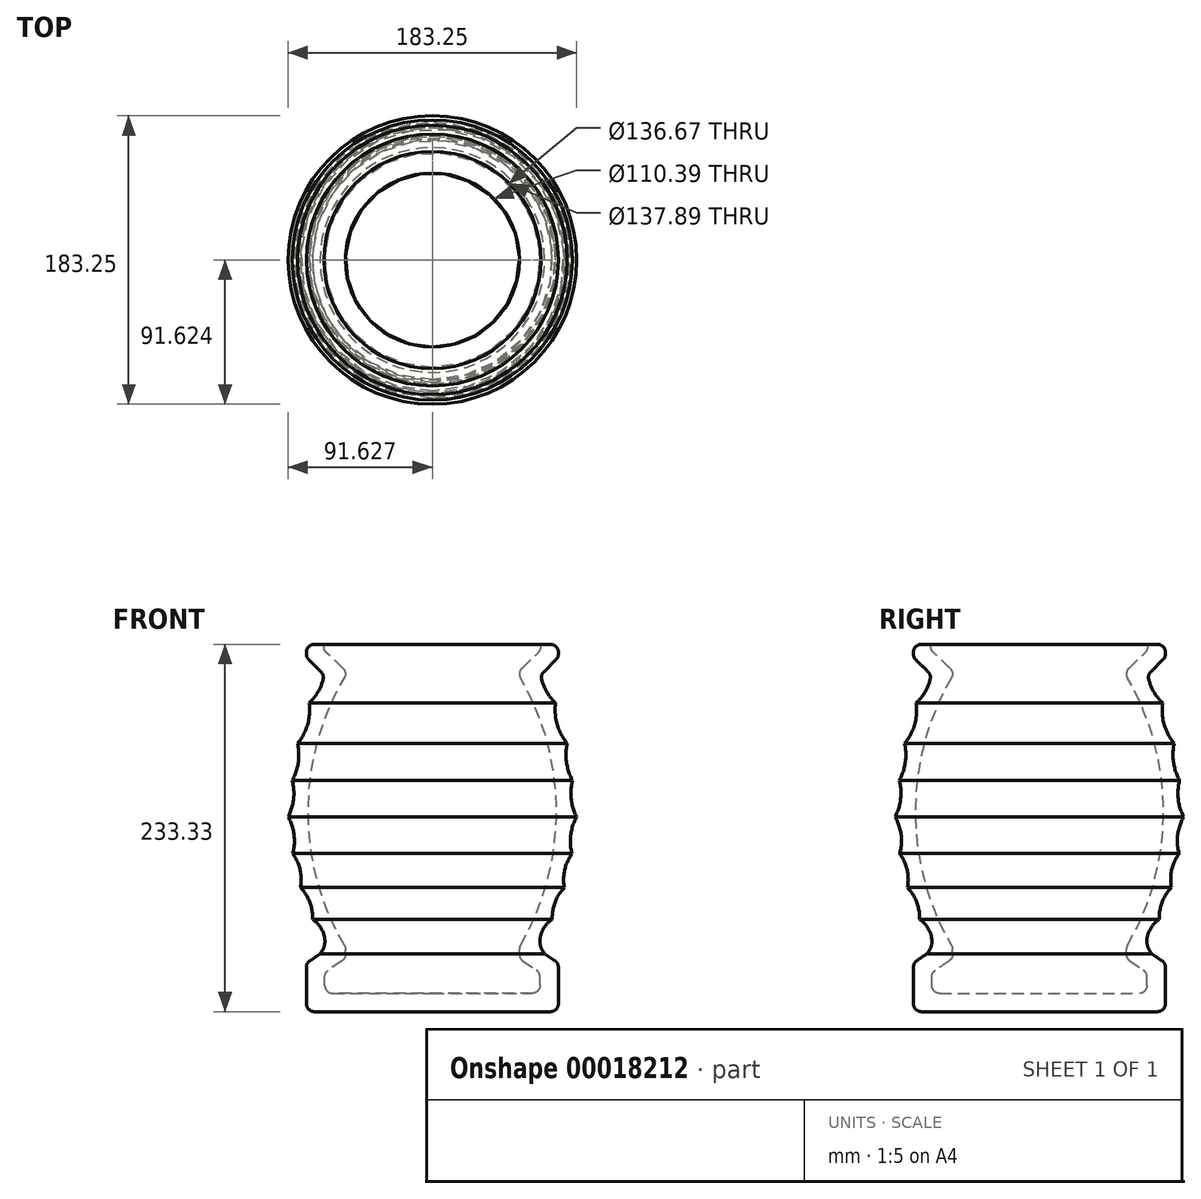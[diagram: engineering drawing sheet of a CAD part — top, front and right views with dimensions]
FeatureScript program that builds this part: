
annotation { "Feature Type Name" : "Feature", "Feature Type Description" : "" }
export const myFeature = defineFeature(function(context is Context, id is Id, definition is map)
    precondition{}
    {
        {
            var Q0;
            Q0=qCreatedBy(makeId("Top.planeOp"),FACE);
            var sketch = newSketch(context, id + "F0", { "sketchPlane" : qUnion([Q0])});
            skLineSegment(sketch, "E0.top", {"start": v(-71, -103.34) * mm, "end": v(4, -103.34) * mm});
            skLineSegment(sketch, "E1", {"start": v(-76, 125) * mm, "end": v(-76, 123.78) * mm});
            skLineSegment(sketch, "E2", {"start": v(-74.51, 120.22) * mm, "end": v(-66.76, 112.58) * mm});
            skLineSegment(sketch, "E3", {"start": v(-76, -98.34) * mm, "end": v(-76, -75.05) * mm});
            skLineSegment(sketch, "E4", {"start": v(-73.82, -70.91) * mm, "end": v(-67.37, -66.52) * mm});
            skLineSegment(sketch, "E5.1", {"start": v(-64.34, -86.67) * mm, "end": v(-64.34, -81.21) * mm});
            skLineSegment(sketch, "E5.2", {"start": v(-62.15, -77.08) * mm, "end": v(-53.38, -71.1) * mm});
            skLineSegment(sketch, "E5.4", {"start": v(-63.4, 124.87) * mm, "end": v(-52.8, 114.77) * mm});
            skArc(sketch, "E5.5", {"start": v(-51.92, 108.64) * mm, "mid": v(-74.82, 23.66) * mm, "end": v(-51.87, -61.3) * mm});
            skLineSegment(sketch, "E5.6", {"start": v(-51.2, -66.97) * mm, "end": v(-51.2, -63.81) * mm});
            skArc(sketch, "E6", {"start": v(-74.28, 92.72) * mm, "mid": v(-68.68, 99.63) * mm, "end": v(-65.4, 107.9) * mm});
            skArc(sketch, "E7", {"start": v(-81.6, 67.04) * mm, "mid": v(-75.23, 79.1) * mm, "end": v(-74.28, 92.72) * mm});
            skLineSegment(sketch, "E8", {"start": v(-64.95, 128.5) * mm, "end": v(-64.95, 128.95) * mm});
            skLineSegment(sketch, "E9", {"start": v(-71, 130) * mm, "end": v(-65.99, 130) * mm});
            skLineSegment(sketch, "E10", {"start": v(-59.34, -91.67) * mm, "end": v(4, -91.67) * mm});
            skLineSegment(sketch, "E11", {"start": v(4, -91.67) * mm, "end": v(4, -103.34) * mm});
            skArc(sketch, "E12", {"start": v(-84.98, 43.55) * mm, "mid": v(-81.2, 55) * mm, "end": v(-81.6, 67.04) * mm});
            skArc(sketch, "E13", {"start": v(-87.63, 20.25) * mm, "mid": v(-84.19, 31.66) * mm, "end": v(-84.98, 43.55) * mm});
            skArc(sketch, "E14", {"start": v(-72.12, -44.65) * mm, "mid": v(-73.9, -33.8) * mm, "end": v(-79.8, -24.54) * mm});
            skArc(sketch, "E15", {"start": v(-79.8, -24.54) * mm, "mid": v(-80.06, -13.23) * mm, "end": v(-84.72, -2.93) * mm});
            skArc(sketch, "E16", {"start": v(-84.72, -2.93) * mm, "mid": v(-83.86, 8.95) * mm, "end": v(-87.63, 20.25) * mm});
            skPoint(sketch, "E17.visualSharp", {"position": v(-76, 130) * mm});
            skArc(sketch, "E17.filletArc", {"start": v(-71, 130) * mm, "mid": v(-74.54, 128.53) * mm, "end": v(-76, 125) * mm});
            skPoint(sketch, "E18.visualSharp", {"position": v(-76, -103.34) * mm});
            skArc(sketch, "E18.filletArc", {"start": v(-76, -98.34) * mm, "mid": v(-74.54, -101.87) * mm, "end": v(-71, -103.34) * mm});
            skPoint(sketch, "E19.visualSharp", {"position": v(-64.34, -91.67) * mm});
            skArc(sketch, "E19.filletArc", {"start": v(-64.34, -86.67) * mm, "mid": v(-62.87, -90.2) * mm, "end": v(-59.34, -91.67) * mm});
            skPoint(sketch, "E20.visualSharp", {"position": v(-64.34, -78.57) * mm});
            skArc(sketch, "E20.filletArc", {"start": v(-62.15, -77.08) * mm, "mid": v(-63.76, -78.88) * mm, "end": v(-64.34, -81.21) * mm});
            skPoint(sketch, "E21.visualSharp", {"position": v(-51.2, -69.61) * mm});
            skArc(sketch, "E21.filletArc", {"start": v(-53.38, -71.1) * mm, "mid": v(-51.78, -69.3) * mm, "end": v(-51.2, -66.97) * mm});
            skPoint(sketch, "E22.visualSharp", {"position": v(-51.2, -62.45) * mm});
            skArc(sketch, "E22.filletArc", {"start": v(-51.2, -63.81) * mm, "mid": v(-51.37, -62.51) * mm, "end": v(-51.87, -61.3) * mm});
            skPoint(sketch, "E23.visualSharp", {"position": v(-76, -72.4) * mm});
            skArc(sketch, "E23.filletArc", {"start": v(-73.82, -70.91) * mm, "mid": v(-75.42, -72.7) * mm, "end": v(-76, -75.05) * mm});
            skPoint(sketch, "E24.visualSharp", {"position": v(-76, 121.69) * mm});
            skArc(sketch, "E24.filletArc", {"start": v(-76, 123.78) * mm, "mid": v(-75.62, 121.85) * mm, "end": v(-74.51, 120.22) * mm});
            skPoint(sketch, "E25.visualSharp", {"position": v(-64.95, 130) * mm});
            skArc(sketch, "E25.filletArc", {"start": v(-64.95, 128.95) * mm, "mid": v(-65.25, 129.7) * mm, "end": v(-65.99, 130) * mm});
            skPoint(sketch, "E26.visualSharp", {"position": v(-49.9, 112.02) * mm});
            skArc(sketch, "E26.filletArc", {"start": v(-51.92, 108.64) * mm, "mid": v(-51.3, 111.86) * mm, "end": v(-52.8, 114.77) * mm});
            skArc(sketch, "E27", {"start": v(-67.37, -66.52) * mm, "mid": v(-64.84, -62.23) * mm, "end": v(-64.34, -57.27) * mm});
            skArc(sketch, "E28", {"start": v(-64.34, -57.27) * mm, "mid": v(-66.86, -50.12) * mm, "end": v(-72.12, -44.65) * mm});
            skPoint(sketch, "E29.visualSharp", {"position": v(-64.95, 126.35) * mm});
            skArc(sketch, "E29.filletArc", {"start": v(-64.95, 128.5) * mm, "mid": v(-64.54, 126.52) * mm, "end": v(-63.4, 124.87) * mm});
            skPoint(sketch, "E30.visualSharp", {"position": v(-64.88, 110.73) * mm});
            skArc(sketch, "E30.filletArc", {"start": v(-65.4, 107.9) * mm, "mid": v(-65.46, 110.41) * mm, "end": v(-66.76, 112.58) * mm});
            skSolve(sketch);
        }
        {
            var Q0;
            Q0=makeQuery(id+"F0.imprint","IMPRINT",FACE,{"disambiguationData":[TD([[makeQuery(id+"F0.imprint","IMPRINT",EDGE,{"derivedFrom":sQuery(id+"F0.wireOp",EDGE,"E0.top")}),1.0]])]});
            var Q1;
            Q1=sQuery(id+"F0.wireOp",EDGE,"E11");
            revolve(context, id + "F1", {"entities" : qUnion([Q0]), "axis" : qUnion([Q1]), "revolveType" : RevolveType.FULL});
        }
        {
            var Q0;
            Q0=makeQuery(id+"F1.opRevolve","SWEPT_BODY",BODY,{"disambiguationData":[OSD([sQuery(id+"F0.wireOp",EDGE,"E0.top"),sQuery(id+"F0.wireOp",EDGE,"E1"),sQuery(id+"F0.wireOp",EDGE,"E2"),sQuery(id+"F0.wireOp",EDGE,"E3"),sQuery(id+"F0.wireOp",EDGE,"E4"),sQuery(id+"F0.wireOp",EDGE,"E5.1"),sQuery(id+"F0.wireOp",EDGE,"E5.2"),sQuery(id+"F0.wireOp",EDGE,"E5.4"),sQuery(id+"F0.wireOp",EDGE,"E5.5"),sQuery(id+"F0.wireOp",EDGE,"E5.6"),sQuery(id+"F0.wireOp",EDGE,"E6"),sQuery(id+"F0.wireOp",EDGE,"E7"),sQuery(id+"F0.wireOp",EDGE,"E8"),sQuery(id+"F0.wireOp",EDGE,"E9"),sQuery(id+"F0.wireOp",EDGE,"E10"),sQuery(id+"F0.wireOp",EDGE,"E11"),sQuery(id+"F0.wireOp",EDGE,"E12"),sQuery(id+"F0.wireOp",EDGE,"E13"),sQuery(id+"F0.wireOp",EDGE,"E14"),sQuery(id+"F0.wireOp",EDGE,"E15"),sQuery(id+"F0.wireOp",EDGE,"E16"),sQuery(id+"F0.wireOp",EDGE,"E17.filletArc"),sQuery(id+"F0.wireOp",EDGE,"E18.filletArc"),sQuery(id+"F0.wireOp",EDGE,"E19.filletArc"),sQuery(id+"F0.wireOp",EDGE,"E20.filletArc"),sQuery(id+"F0.wireOp",EDGE,"E21.filletArc"),sQuery(id+"F0.wireOp",EDGE,"E22.filletArc"),sQuery(id+"F0.wireOp",EDGE,"E23.filletArc"),sQuery(id+"F0.wireOp",EDGE,"E24.filletArc"),sQuery(id+"F0.wireOp",EDGE,"E25.filletArc"),sQuery(id+"F0.wireOp",EDGE,"E26.filletArc"),sQuery(id+"F0.wireOp",EDGE,"E27"),sQuery(id+"F0.wireOp",EDGE,"E28"),sQuery(id+"F0.wireOp",EDGE,"E29.filletArc"),sQuery(id+"F0.wireOp",EDGE,"E30.filletArc")])]});
            var Q1;
            Q1=sQuery(id+"F0.wireOp",EDGE,"E0.top");
            transform(context, id + "F2", {"entities" : qUnion([Q0]), "transformType" : TransformType.ROTATION, "transformAxis" : qUnion([Q1]), "angle" : 90 * degree, "makeCopy" : false});
        }
    });
